# Revit family: Shower-Handshower-KOHLER-Statement_Round-K-R28694T_1
name_source: partatom
category: Plumbing Fixtures
units: mm (PartAtom-declared; Revit-internal decimal feet)

## family parameters
Cut with Voids When Loaded = No
Host = Face
OmniClass Number = 23.31.17.00
OmniClass Title = Showers
Part Type = Normal
Room Calculation Point = No
Round Connector Dimension = Use Diameter
Shared = No

## types (3) — shared parameters
ADA Compliant = No
Assembly Code = D2010700
CW Connection = No
Cold Water Inlet = Cold Water Inlet
Date Modified = 01/23/2023
Drain Included = No
Finish = Kohler-Plastic-CP-Polished_Chrome
HW Connection = Yes
Height = 9"
Hot Water Inlet = Hot Water Inlet
Length = 3 1/8"
Manufacturer = Kohler Co.
Master Format 2014 = 22 42 23
Master Format 2014 Name = Residential Showers
Material = Plastic
Panel Thickness = 0"
Pressure = 80.00 psi
Product Name = Statement Round
Tempered Water Inlet = Tempered Water Inlet
URL = http://www.kohler.com.cn
Vent Connection = No
Waste Connection = No
Waste Water Outlet = Waste Water Outlet
WaterSense Certified = No
Width = 5 1/8"

## per-type parameters (varying)
| type | Default Elevation | Description | Flow Rate | Model | Type |
| 2.5GPM, CP-Polished Chrome | 45" | Round Handshower With Watermind | 3 GPM | K-R28694T-CP | 1 |
| 1.5GPM, CP-Polished Chrome | 42" | Round Handshower With Watermind | 2 GPM | K-R28694T-E2-CP | 2 |
| 1.32GPM, CP-Polished Chrome | 42" | Round Handshower With Watermind 1.32GPM | 1 GPM | K-R28694T-E3-CP | 3 |

## geometry (parser evidence)
native form markers: Sweep x6
no freeform markers — native parametric forms only
